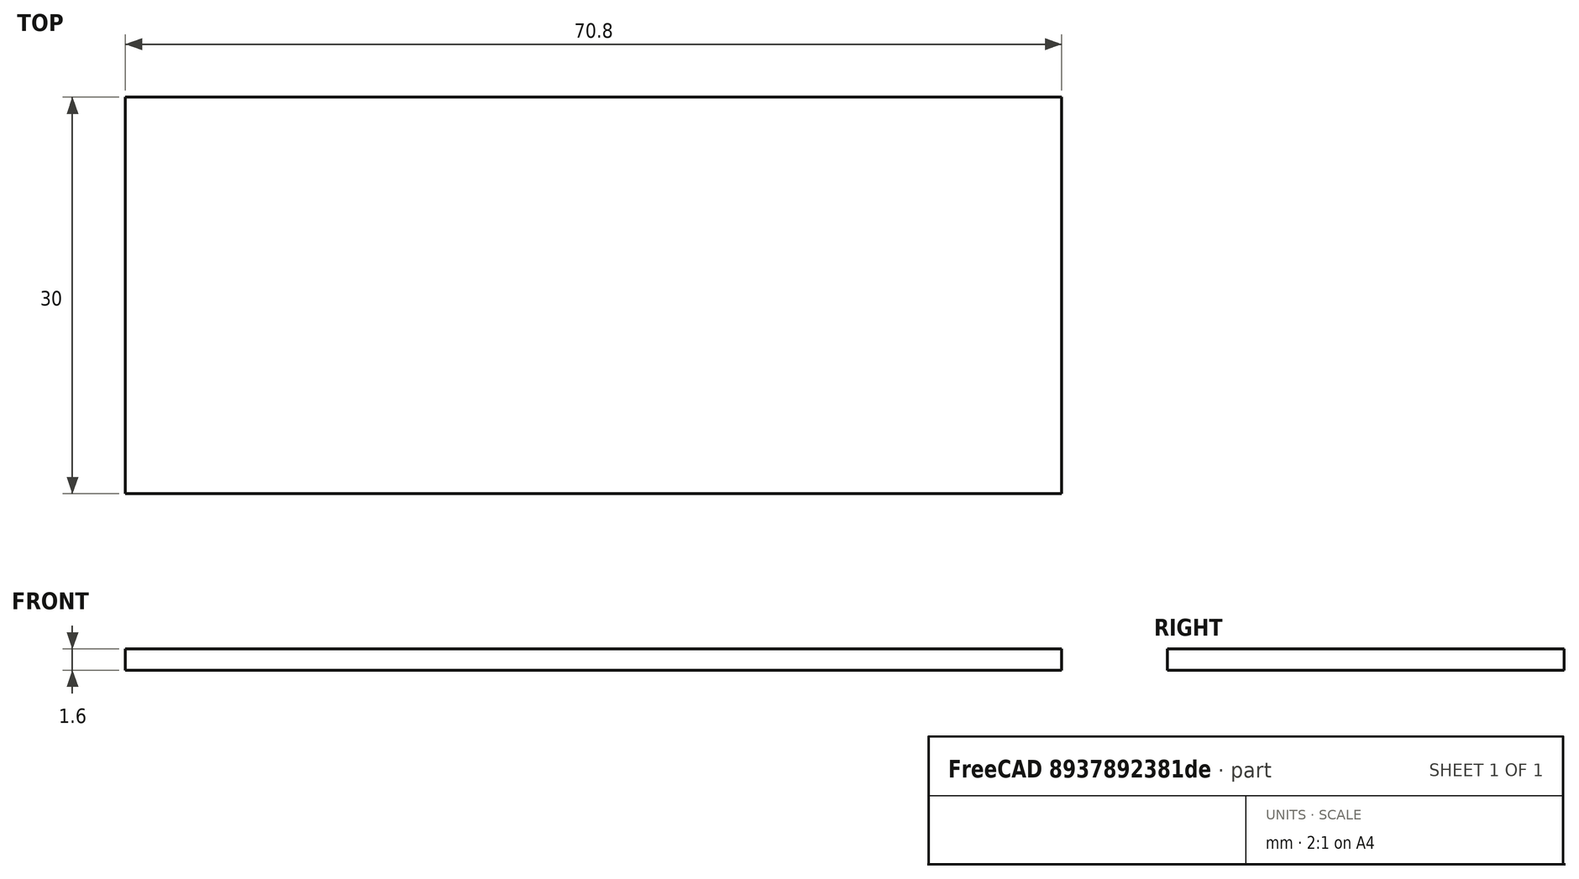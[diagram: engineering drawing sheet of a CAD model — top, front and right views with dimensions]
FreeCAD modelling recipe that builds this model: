
FCSTD DOCUMENT  (FreeCAD 0.19R24276 (Git))
Label: pir-baffel-bottomBack
License: All rights reserved
LicenseURL: http://en.wikipedia.org/wiki/All_rights_reserved
objects: Sketcher::SketchObject×1, PartDesign::Pad×1, PartDesign::CoordinateSystem×1, PartDesign::Body×1
note: 5 computed .brp shape members not serialized (recipe doc carries the construction recipe); baked Part::Feature solids carry a one-line shape summary decoded from their .brp

FEATURE [Sketcher::SketchObject] Sketch
  FullyConstrained = true
  MapMode = 5
  Support = -> [XY_Plane]
  sketch-geometry (4):
    g0: LineSegment StartX=-35.4 StartY=15 StartZ=0 EndX=35.4 EndY=15 EndZ=0
    g1: LineSegment StartX=35.4 StartY=15 StartZ=0 EndX=35.4 EndY=-15 EndZ=0
    g2: LineSegment StartX=35.4 StartY=-15 StartZ=0 EndX=-35.4 EndY=-15 EndZ=0
    g3: LineSegment StartX=-35.4 StartY=-15 StartZ=0 EndX=-35.4 EndY=15 EndZ=0
  constraints (10):
    c: Coincident(g0,g1)
    c: Coincident(g1,g2)
    c: Coincident(g2,g3)
    c: Coincident(g3,g0)
    c: Horizontal(g2)
    c: Vertical(g3)
    c: DistanceY(g3,g3) = 30
    c: DistanceX(g0,g0) = 70.8
    c: Symmetric(g0,g0,g-2)
    c: Symmetric(g0,g1,g-1)
FEATURE [PartDesign::Pad] Pad  label="BottomBack"
  Direction = (1,1,1)
  Length = 1.6
  Length2 = 100
  Profile = -> Sketch
  Type = 0
FEATURE [PartDesign::CoordinateSystem] LCS_bottomBack
  AttacherType = Attacher::AttachEngine3D
  MapMode = 45
  Placement = pos=(2e-16,3e-16,1.6) rot=(0,0,1;1.5708rad)
  Support = -> [Pad]
FEATURE [PartDesign::Body] Body
  Group = -> [Sketch,Pad,LCS_bottomBack]
  Origin = -> Origin
  Tip = -> Pad
